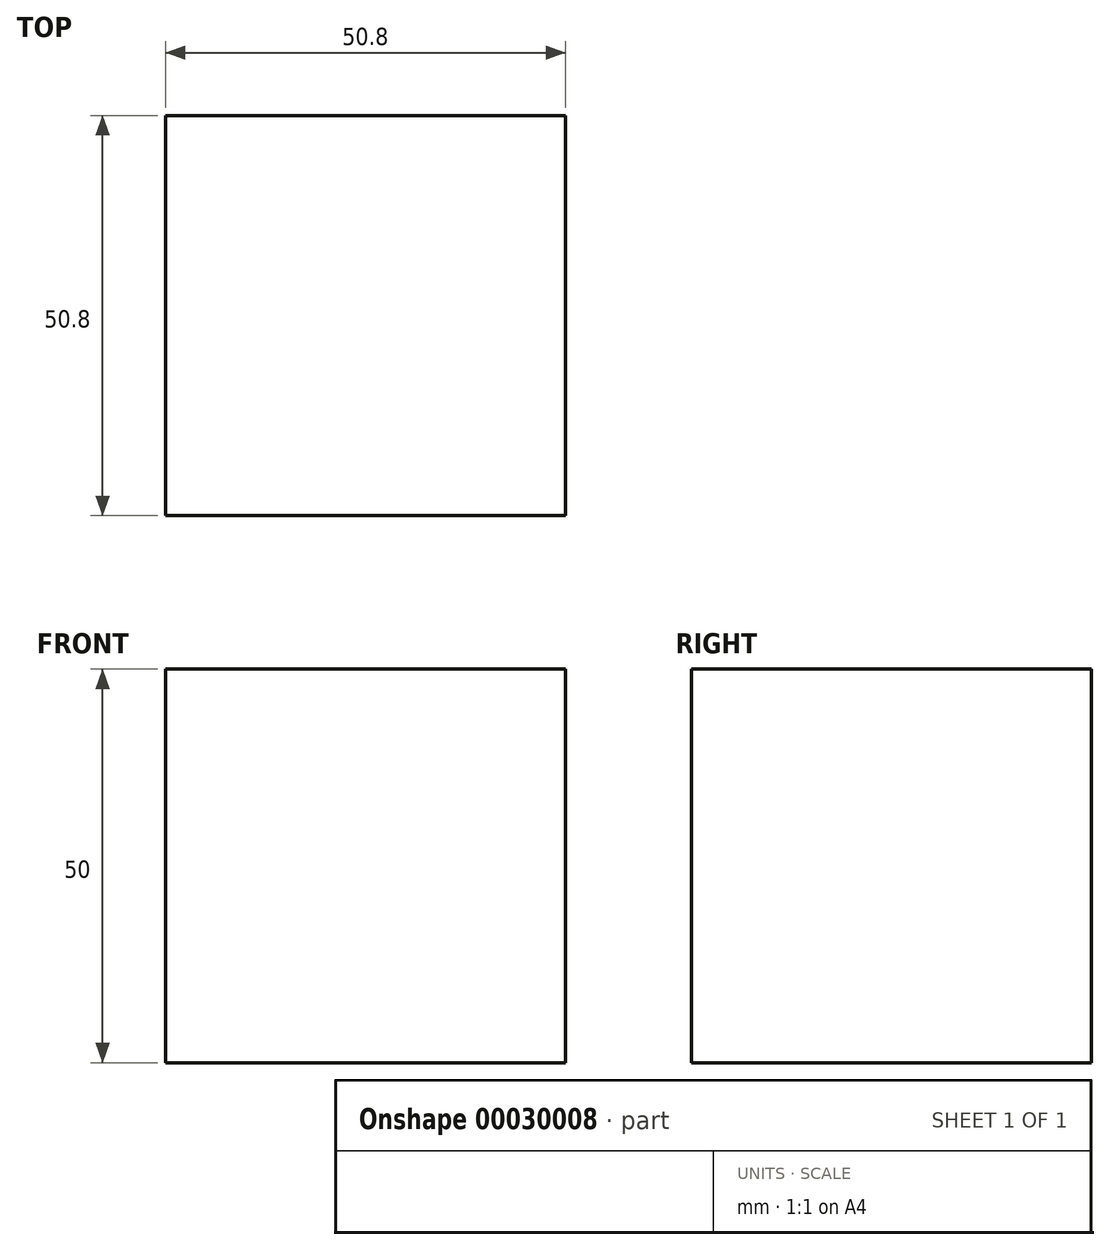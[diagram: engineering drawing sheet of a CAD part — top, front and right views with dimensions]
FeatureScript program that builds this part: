
annotation { "Feature Type Name" : "Feature", "Feature Type Description" : "" }
export const myFeature = defineFeature(function(context is Context, id is Id, definition is map)
    precondition{}
    {
        {
            var Q0;
            Q0=qCreatedBy(makeId("Top.planeOp"),FACE);
            var sketch = newSketch(context, id + "F0", { "sketchPlane" : qUnion([Q0])});
            skLineSegment(sketch, "E0.bottom", {"start": v(-25.4, 25.4) * mm, "end": v(25.4, 25.4) * mm});
            skLineSegment(sketch, "E0.top", {"start": v(-25.4, -25.4) * mm, "end": v(25.4, -25.4) * mm});
            skLineSegment(sketch, "E0.left", {"start": v(-25.4, 25.4) * mm, "end": v(-25.4, -25.4) * mm});
            skLineSegment(sketch, "E0.right", {"start": v(25.4, 25.4) * mm, "end": v(25.4, -25.4) * mm});
            skSolve(sketch);
        }
        {
            var Q0;
            Q0 = qSketchRegion(id + "F0", true);
            extrude(context, id + "F1", {"entities" : qUnion([Q0]), "depth" : 50 * mm});
        }
    });
